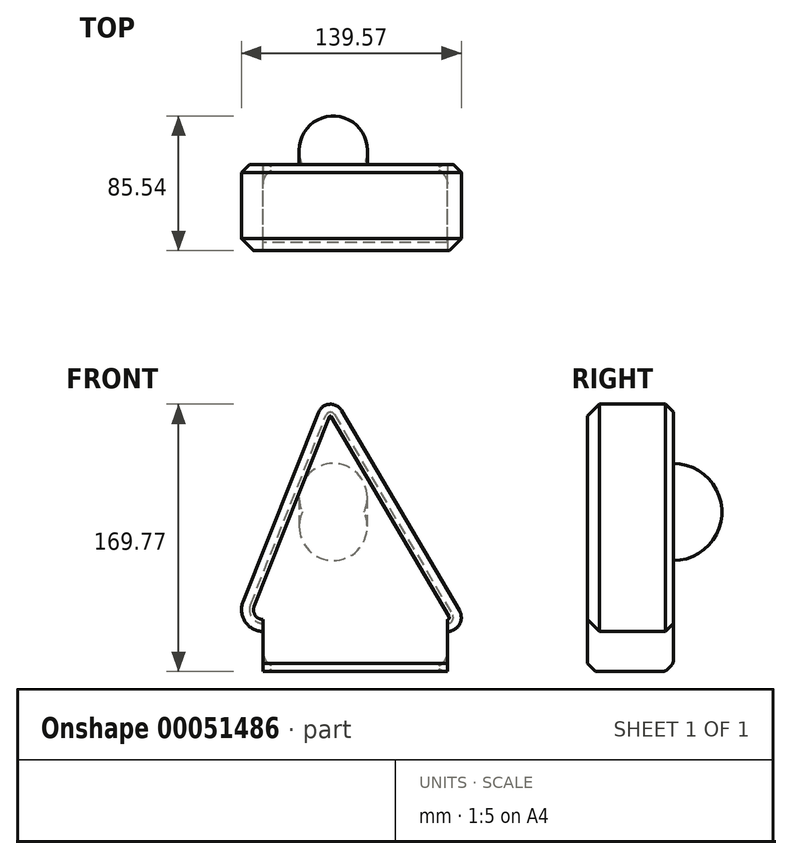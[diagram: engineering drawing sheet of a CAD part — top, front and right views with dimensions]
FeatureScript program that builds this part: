
annotation { "Feature Type Name" : "Feature", "Feature Type Description" : "" }
export const myFeature = defineFeature(function(context is Context, id is Id, definition is map)
    precondition{}
    {
        {
            var Q0;
            Q0=qCreatedBy(makeId("Front.planeOp"),FACE);
            var sketch = newSketch(context, id + "F0", { "sketchPlane" : qUnion([Q0])});
            skLineSegment(sketch, "E0", {"start": v(-13.98, 78.75) * mm, "end": v(77.14, -75.88) * mm});
            skLineSegment(sketch, "E1", {"start": v(77.14, -75.88) * mm, "end": v(-75.6, -75.88) * mm});
            skLineSegment(sketch, "E2", {"start": v(-75.6, -75.88) * mm, "end": v(-13.98, 78.75) * mm});
            skSolve(sketch);
        }
        {
            var Q0;
            Q0 = qSketchRegion(id + "F0", true);
            extrude(context, id + "F1", {"entities" : qUnion([Q0]), "depth" : 54.73 * mm});
        }
        {
            var Q0;
            Q0=makeQuery(id+"F1.opExtrude","SWEPT_EDGE",EDGE,{"disambiguationData":[OSD([sQuery(id+"F0.wireOp",EDGE,"E0"),sQuery(id+"F0.wireOp",EDGE,"E1")])]});
            fillet(context, id + "F2", {"entities" : qUnion([Q0]), "radius" : 8.83 * mm, "tangentPropagation" : true, "allowEdgeOverflow" : false});
        }
        {
            var Q0;
            Q0=makeQuery(id+"F1.opExtrude","SWEPT_EDGE",EDGE,{"disambiguationData":[OSD([sQuery(id+"F0.wireOp",EDGE,"E1"),sQuery(id+"F0.wireOp",EDGE,"E2")])]});
            fillet(context, id + "F3", {"entities" : qUnion([Q0]), "radius" : 13.78 * mm, "tangentPropagation" : true, "allowEdgeOverflow" : false});
        }
        {
            var Q0;
            Q0=makeQuery(id+"F1.opExtrude","SWEPT_EDGE",EDGE,{"disambiguationData":[OSD([sQuery(id+"F0.wireOp",EDGE,"E0"),sQuery(id+"F0.wireOp",EDGE,"E2")])]});
            fillet(context, id + "F4", {"entities" : qUnion([Q0]), "radius" : 8.1 * mm, "tangentPropagation" : true, "allowEdgeOverflow" : false});
        }
        {
            var Q0;
            Q0=qCreatedBy(makeId("Top.planeOp"),FACE);
            var sketch = newSketch(context, id + "F5", { "sketchPlane" : qUnion([Q0])});
            skLineSegment(sketch, "E3.0", {"start": v(-13.98, 0) * mm, "end": v(77.14, 0) * mm, "construction": true});
            skLineSegment(sketch, "E4.0", {"start": v(-75.6, 0) * mm, "end": v(-13.98, 0) * mm});
            skArc(sketch, "E5", {"start": v(-30.34, 0) * mm, "mid": v(-10.79, -30.8) * mm, "end": v(8.76, 0) * mm});
            skLineSegment(sketch, "E6", {"start": v(-30.34, 0) * mm, "end": v(8.76, 0) * mm});
            skSolve(sketch);
        }
        {
            var Q0;
            Q0 = qSketchRegion(id + "F5", true);
            var Q1;
            Q1=sQuery(id+"F5.wireOp",EDGE,"E3.0");
            revolve(context, id + "F6", {"operationType" : NewBodyOperationType.ADD, "entities" : qUnion([Q0]), "axis" : qUnion([Q1]), "revolveType" : RevolveType.FULL});
        }
        {
            var Q0;
            Q0=makeQuery(id+"F1.opExtrude","SWEPT_FACE",FACE,{"disambiguationData":[OSD([sQuery(id+"F0.wireOp",EDGE,"E1")])]});
            var sketch = newSketch(context, id + "F7", { "sketchPlane" : qUnion([Q0])});
            skLineSegment(sketch, "E7.0", {"start": v(-55.27, 54.73) * mm, "end": v(-55.27, 0) * mm});
            skLineSegment(sketch, "E8.0", {"start": v(61.68, 0) * mm, "end": v(-55.27, 0) * mm});
            skLineSegment(sketch, "E9.0", {"start": v(61.68, 0) * mm, "end": v(61.68, 54.73) * mm});
            skLineSegment(sketch, "E10.0", {"start": v(61.68, 54.73) * mm, "end": v(-55.27, 54.73) * mm});
            skPoint(sketch, "E11.orphan", {"position": v(77.14, 0) * mm});
            skPoint(sketch, "E12.orphan", {"position": v(-75.6, 0) * mm});
            skSolve(sketch);
        }
        {
            var Q0;
            Q0 = qSketchRegion(id + "F7", true);
            extrude(context, id + "F8", {"entities" : qUnion([Q0]), "operationType" : NewBodyOperationType.ADD, "depth" : 25.4 * mm});
        }
        {
            var Q0;
            Q0=makeQuery(id+"F1.opExtrude","CAP_EDGE",EDGE,{"disambiguationData":[OSD([sQuery(id+"F0.wireOp",EDGE,"E0")])],"isStart":false});
            chamfer(context, id + "F9", {"entities" : qUnion([Q0]), "width" : 7.62 * mm, "tangentPropagation" : true});
        }
        {
            var Q0;
            Q0=makeQuery(id+"F1.opExtrude","CAP_EDGE",EDGE,{"disambiguationData":[OSD([sQuery(id+"F0.wireOp",EDGE,"E0")])],"isStart":true});
            chamfer(context, id + "F10", {"entities" : qUnion([Q0]), "width" : 5.08 * mm, "tangentPropagation" : true});
        }
        {
            var Q0;
            Q0=makeQuery(id+"F8.opExtrude","CAP_EDGE",EDGE,{"disambiguationData":[OSD([sQuery(id+"F7.wireOp",EDGE,"E8.0")])],"isStart":false});
            chamfer(context, id + "F11", {"entities" : qUnion([Q0]), "width" : 5.08 * mm, "tangentPropagation" : true});
        }
        {
            var Q0;
            Q0=makeQuery(id+"F11.opChamfer","BLEND_FACE",FACE,{"disambiguationData":[OSD([sQuery(id+"F7.wireOp",EDGE,"E8.0")])]});
            fillet(context, id + "F12", {"entities" : qUnion([Q0]), "radius" : 5.08 * mm, "tangentPropagation" : true, "allowEdgeOverflow" : false});
        }
        {
            var Q0;
            Q0=makeQuery(id+"F8.opExtrude","CAP_EDGE",EDGE,{"disambiguationData":[OSD([sQuery(id+"F7.wireOp",EDGE,"E10.0")])],"isStart":false});
            chamfer(context, id + "F13", {"entities" : qUnion([Q0]), "width" : 5.08 * mm, "tangentPropagation" : true});
        }
    });
